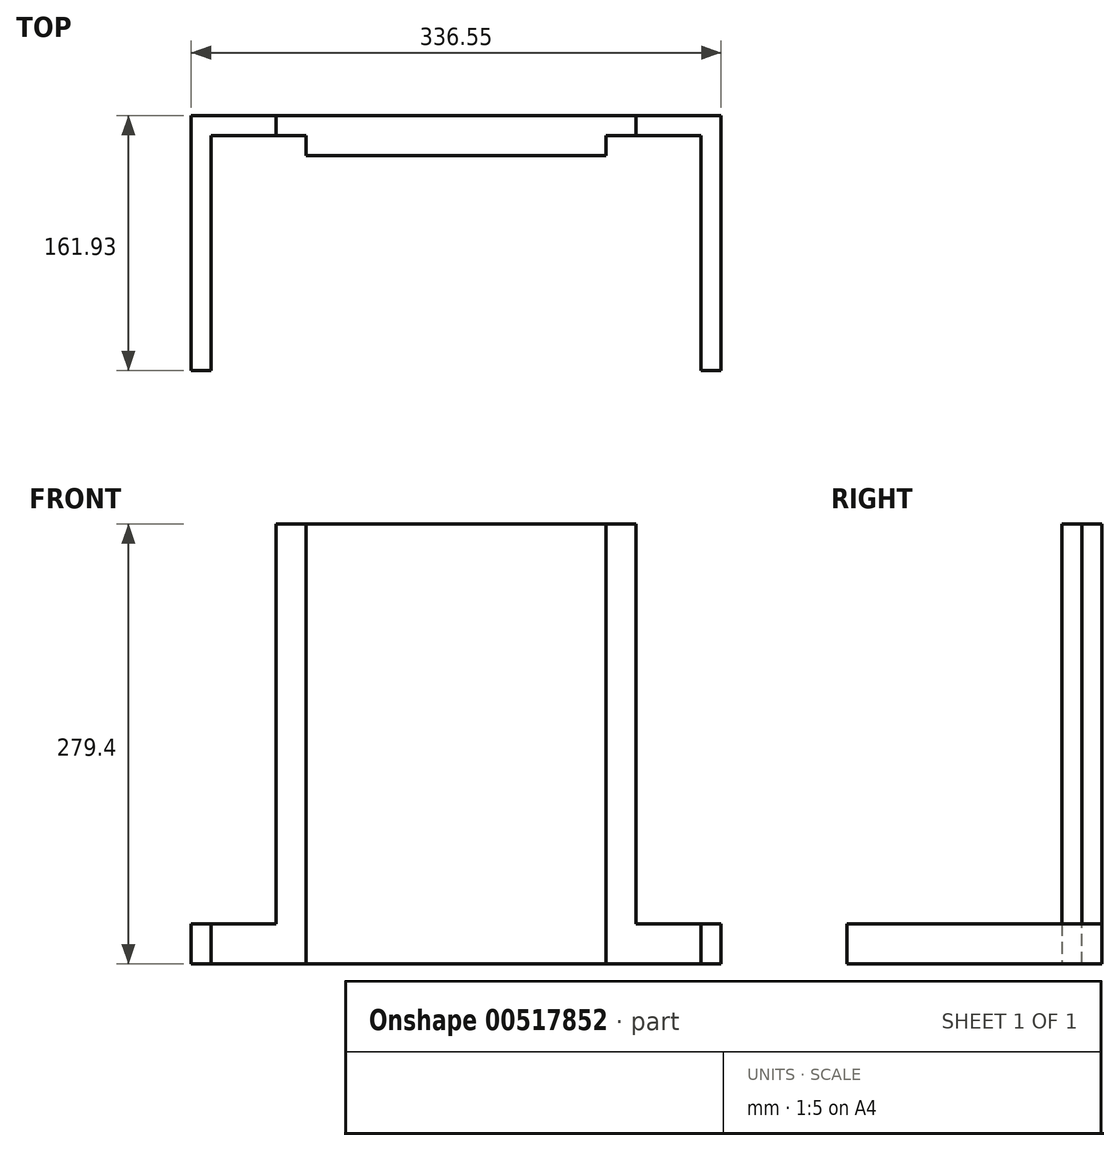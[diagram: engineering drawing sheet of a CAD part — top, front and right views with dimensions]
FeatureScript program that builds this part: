
annotation { "Feature Type Name" : "Feature", "Feature Type Description" : "" }
export const myFeature = defineFeature(function(context is Context, id is Id, definition is map)
    precondition{}
    {
        {
            var Q0;
            Q0=qCreatedBy(makeId("Top.planeOp"),FACE);
            var sketch = newSketch(context, id + "F0", { "sketchPlane" : qUnion([Q0])});
            skLineSegment(sketch, "E0", {"start": v(-165.91, 0) * mm, "end": v(-165.91, -161.93) * mm});
            skLineSegment(sketch, "E1", {"start": v(-165.91, -161.93) * mm, "end": v(-153.21, -161.93) * mm});
            skLineSegment(sketch, "E2", {"start": v(-153.21, -161.93) * mm, "end": v(-153.21, -25.4) * mm});
            skLineSegment(sketch, "E3", {"start": v(-153.21, -25.4) * mm, "end": v(157.94, -25.4) * mm});
            skLineSegment(sketch, "E4", {"start": v(157.94, -25.4) * mm, "end": v(157.94, -161.93) * mm});
            skLineSegment(sketch, "E5", {"start": v(157.94, -161.93) * mm, "end": v(170.64, -161.93) * mm});
            skLineSegment(sketch, "E6", {"start": v(-165.91, 0) * mm, "end": v(170.64, 0) * mm});
            skLineSegment(sketch, "E7", {"start": v(170.64, 0) * mm, "end": v(170.64, -161.92) * mm});
            skSolve(sketch);
        }
        {
            var Q0;
            Q0 = qSketchRegion(id + "F0", true);
            extrude(context, id + "F1", {"entities" : qUnion([Q0]), "depth" : 25.4 * mm, "offsetDistance" : 25.4 * mm});
        }
        {
            var Q0;
            Q0=makeQuery(id+"F1.opExtrude","CAP_FACE",FACE,{"disambiguationData":[OSD([sQuery(id+"F0.wireOp",EDGE,"E0"),sQuery(id+"F0.wireOp",EDGE,"E1"),sQuery(id+"F0.wireOp",EDGE,"E2"),sQuery(id+"F0.wireOp",EDGE,"E3"),sQuery(id+"F0.wireOp",EDGE,"E4"),sQuery(id+"F0.wireOp",EDGE,"E5"),sQuery(id+"F0.wireOp",EDGE,"E6"),sQuery(id+"F0.wireOp",EDGE,"E7")])],"isStart":false});
            var sketch = newSketch(context, id + "F2", { "sketchPlane" : qUnion([Q0])});
            skLineSegment(sketch, "E8.bottom", {"start": v(-92.89, 0) * mm, "end": v(97.61, 0) * mm});
            skLineSegment(sketch, "E8.top", {"start": v(-92.89, -25.4) * mm, "end": v(97.61, -25.4) * mm});
            skLineSegment(sketch, "E8.left", {"start": v(-92.89, 0) * mm, "end": v(-92.89, -25.4) * mm});
            skLineSegment(sketch, "E8.right", {"start": v(97.61, 0) * mm, "end": v(97.61, -25.4) * mm});
            skLineSegment(sketch, "E9.bottom", {"start": v(116.66, 0) * mm, "end": v(-111.94, 0) * mm});
            skLineSegment(sketch, "E9.top", {"start": v(116.66, -12.7) * mm, "end": v(-111.94, -12.7) * mm});
            skLineSegment(sketch, "E9.left", {"start": v(116.66, 0) * mm, "end": v(116.66, -12.7) * mm});
            skLineSegment(sketch, "E9.right", {"start": v(-111.94, 0) * mm, "end": v(-111.94, -12.7) * mm});
            skLineSegment(sketch, "E10.bottom", {"start": v(97.61, -25.4) * mm, "end": v(157.94, -25.4) * mm});
            skLineSegment(sketch, "E10.top", {"start": v(97.61, -12.7) * mm, "end": v(157.94, -12.7) * mm});
            skLineSegment(sketch, "E10.left", {"start": v(97.61, -25.4) * mm, "end": v(97.61, -12.7) * mm});
            skLineSegment(sketch, "E10.right", {"start": v(157.94, -25.4) * mm, "end": v(157.94, -12.7) * mm});
            skLineSegment(sketch, "E11.bottom", {"start": v(-92.89, -25.4) * mm, "end": v(-153.21, -25.4) * mm});
            skLineSegment(sketch, "E11.top", {"start": v(-92.89, -12.7) * mm, "end": v(-153.21, -12.7) * mm});
            skLineSegment(sketch, "E11.left", {"start": v(-92.89, -25.4) * mm, "end": v(-92.89, -12.7) * mm});
            skLineSegment(sketch, "E11.right", {"start": v(-153.21, -25.4) * mm, "end": v(-153.21, -12.7) * mm});
            skSolve(sketch);
        }
        {
            var Q0;
            Q0=makeQuery(id+"F2.imprint","IMPRINT",FACE,{"disambiguationData":[TD([[makeQuery(id+"F2.imprint","IMPRINT",EDGE,{"derivedFrom":sQuery(id+"F2.wireOp",EDGE,"E8.top")}),1.0]])]});
            var Q1;
            {var subQ0=sQuery(id+"F2.wireOp",EDGE,"E8.left");Q1=makeQuery(id+"F2.imprint","IMPRINT",FACE,{"disambiguationData":[TD([[makeQuery(id+"F2.imprint","IMPRINT",EDGE,{"derivedFrom":subQ0}),1.0]])]});}
            var Q2;
            {var subQ0=sQuery(id+"F2.wireOp",EDGE,"E8.left");Q2=makeQuery(id+"F2.imprint","IMPRINT",FACE,{"disambiguationData":[TD([[makeQuery(id+"F2.imprint","IMPRINT",EDGE,{"derivedFrom":subQ0}),-1.0]])]});}
            var Q3;
            {var subQ0=sQuery(id+"F2.wireOp",EDGE,"E8.right");Q3=makeQuery(id+"F2.imprint","IMPRINT",FACE,{"disambiguationData":[TD([[makeQuery(id+"F2.imprint","IMPRINT",EDGE,{"derivedFrom":subQ0}),1.0]])]});}
            extrude(context, id + "F3", {"entities" : qUnion([Q0, Q1, Q2, Q3]), "operationType" : NewBodyOperationType.ADD, "depth" : 254 * mm, "offsetDistance" : 25.4 * mm});
        }
        {
            var Q0;
            Q0=makeQuery(id+"F2.imprint","IMPRINT",FACE,{"disambiguationData":[TD([[makeQuery(id+"F2.imprint","IMPRINT",EDGE,{"derivedFrom":sQuery(id+"F2.wireOp",EDGE,"E10.bottom")}),1.0]])]});
            var Q1;
            Q1=makeQuery(id+"F2.imprint","IMPRINT",FACE,{"disambiguationData":[TD([[makeQuery(id+"F2.imprint","IMPRINT",EDGE,{"derivedFrom":sQuery(id+"F2.wireOp",EDGE,"E11.bottom")}),1.0]])]});
            extrude(context, id + "F4", {"entities" : qUnion([Q0, Q1]), "operationType" : NewBodyOperationType.REMOVE, "oppositeDirection" : true, "depth" : 25.4 * mm, "offsetDistance" : 25.4 * mm});
        }
    });
